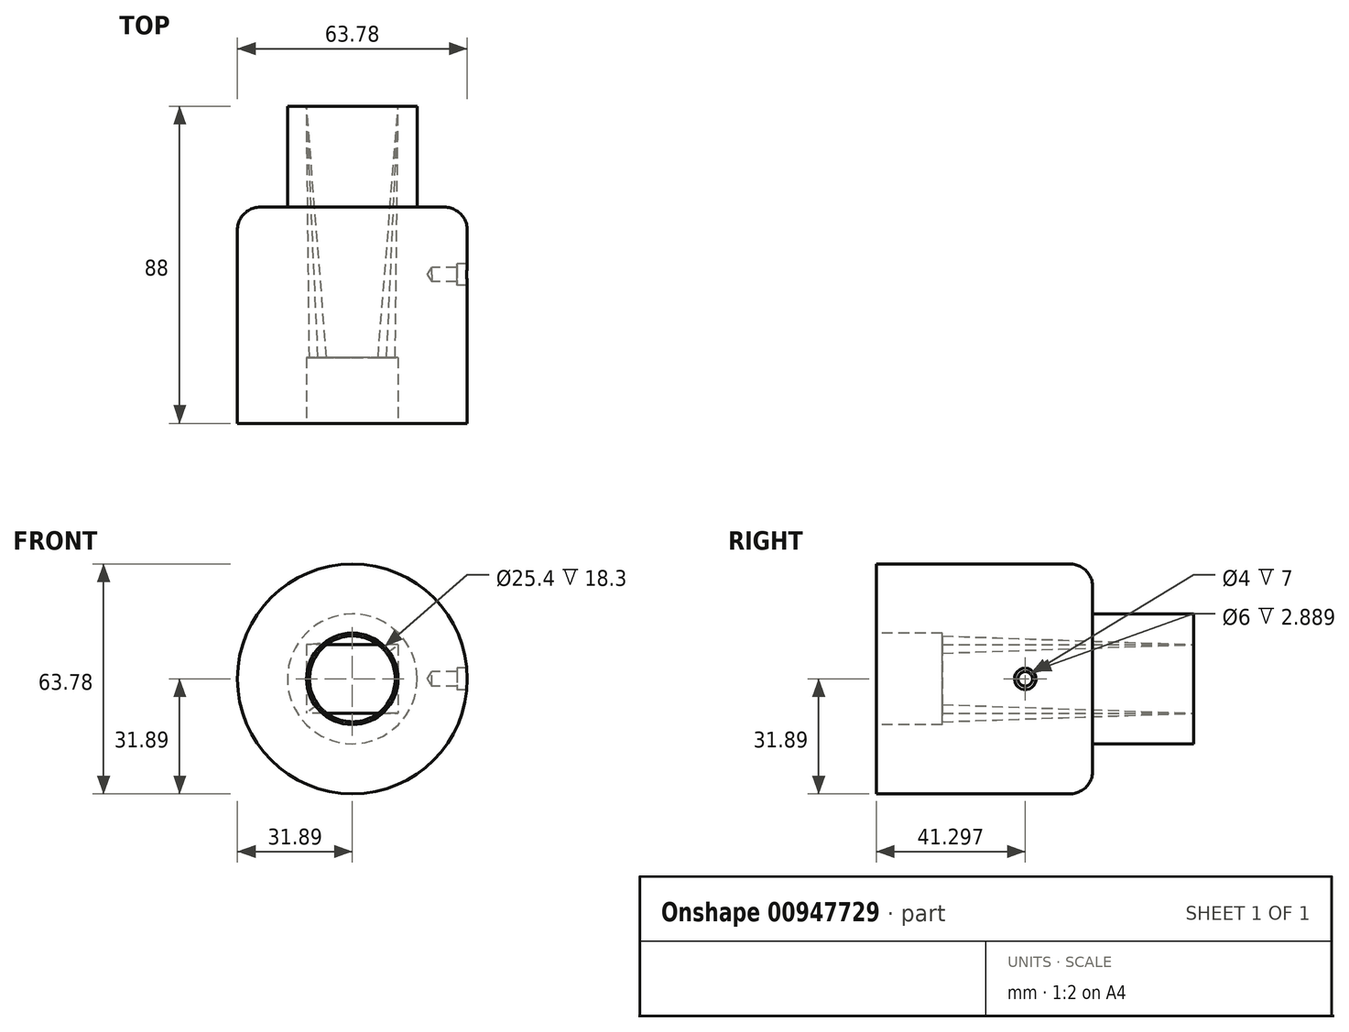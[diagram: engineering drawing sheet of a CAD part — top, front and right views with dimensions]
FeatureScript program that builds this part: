
annotation { "Feature Type Name" : "Feature", "Feature Type Description" : "" }
export const myFeature = defineFeature(function(context is Context, id is Id, definition is map)
    precondition{}
    {
        {
            var Q0;
            Q0=qCreatedBy(makeId("Right.planeOp"),FACE);
            var sketch = newSketch(context, id + "F0", { "sketchPlane" : qUnion([Q0])});
            skLineSegment(sketch, "E0", {"start": v(-91.81, 0) * mm, "end": v(-91.81, 31.89) * mm});
            skLineSegment(sketch, "E1", {"start": v(-91.81, 31.89) * mm, "end": v(-38.16, 31.89) * mm});
            skLineSegment(sketch, "E2", {"start": v(-91.81, 0) * mm, "end": v(-3.81, 0) * mm});
            skLineSegment(sketch, "E3", {"start": v(-3.81, 0) * mm, "end": v(-3.81, 18) * mm});
            skLineSegment(sketch, "E4", {"start": v(-3.81, 18) * mm, "end": v(-31.81, 18) * mm});
            skLineSegment(sketch, "E5", {"start": v(-31.81, 18) * mm, "end": v(-31.81, 25.54) * mm});
            skPoint(sketch, "E6.visualSharp", {"position": v(-31.81, 31.89) * mm});
            skArc(sketch, "E6.filletArc", {"start": v(-31.81, 25.54) * mm, "mid": v(-33.67, 30.03) * mm, "end": v(-38.16, 31.89) * mm});
            skSolve(sketch);
        }
        {
            var Q0;
            Q0=qSketchRegion(id+"F0",true);
            var Q1;
            Q1=sQuery(id+"F0.wireOp",EDGE,"E2");
            revolve(context, id + "F1", {"entities" : qUnion([Q0]), "axis" : qUnion([Q1]), "revolveType" : RevolveType.FULL});
        }
        {
            var Q0;
            Q0=makeQuery(id+"F1.opRevolve","SWEPT_FACE",FACE,{"disambiguationData":[OSD([sQuery(id+"F0.wireOp",EDGE,"E3")])]});
            var sketch = newSketch(context, id + "F2", { "sketchPlane" : qUnion([Q0])});
            skLineSegment(sketch, "E7.bottom", {"start": v(-12.7, 9.52) * mm, "end": v(12.7, 9.52) * mm});
            skLineSegment(sketch, "E7.top", {"start": v(-12.7, -9.53) * mm, "end": v(12.7, -9.53) * mm});
            skLineSegment(sketch, "E7.left", {"start": v(-12.7, 9.52) * mm, "end": v(-12.7, -9.52) * mm});
            skLineSegment(sketch, "E7.right", {"start": v(12.7, 9.52) * mm, "end": v(12.7, -9.53) * mm});
            skSolve(sketch);
        }
        {
            var Q0;
            Q0=makeQuery(id+"F1.opRevolve","SWEPT_FACE",FACE,{"disambiguationData":[OSD([sQuery(id+"F0.wireOp",EDGE,"E0")])]});
            var sketch = newSketch(context, id + "F3", { "sketchPlane" : qUnion([Q0])});
            skCircle(sketch, "E8", {"center": v(0, 0) * mm, "radius": 12.7 * mm});
            skSolve(sketch);
        }
        {
            var Q0;
            Q0=qSketchRegion(id+"F3",true);
            extrude(context, id + "F4", {"entities" : qUnion([Q0]), "operationType" : NewBodyOperationType.REMOVE, "oppositeDirection" : true, "depth" : 18.3 * mm});
        }
        {
            var Q0;
            Q0=makeQuery(id+"F4.boolean.opBoolean","COPY",FACE,{"derivedFrom":makeQuery(id+"F4.opExtrude","CAP_FACE",FACE,{"disambiguationData":[OSD([sQuery(id+"F3.wireOp",EDGE,"E8")])],"isStart":false})});
            var sketch = newSketch(context, id + "F5", { "sketchPlane" : qUnion([Q0])});
            skCircle(sketch, "E9", {"center": v(0, 0) * mm, "radius": 11.9 * mm});
            skSolve(sketch);
        }
        {
            var Q1;
            Q1=qSketchRegion(id+"F5",true);
            var Q2;
            Q2=qSketchRegion(id+"F2",true);
            loft(context, id + "F6", {"operationType" : NewBodyOperationType.REMOVE, "sheetProfilesArray" : [{ "sheetProfileEntities" : qUnion([Q1]) }, { "sheetProfileEntities" : qUnion([Q2]) }]});
        }
        {
            var Q0;
            Q0=qCreatedBy(makeId("Right.planeOp"),FACE);
            cPlane(context, id + "F7", {"entities" : qUnion([Q0]), "cplaneType" : CPlaneType.OFFSET, "offset" : 32 * mm, "width" : 150 * mm, "height" : 150 * mm});
        }
        {
            var Q0;
            Q0=qCreatedBy(id+"F7.planeOp",FACE);
            var sketch = newSketch(context, id + "F8", { "sketchPlane" : qUnion([Q0])});
            skLineSegment(sketch, "E10", {"start": v(0, 0) * mm, "end": v(-115.51, 0) * mm, "construction": true});
            skPoint(sketch, "E11", {"position": v(-50.51, 0) * mm});
            skSolve(sketch);
        }
        {
            var Q0;
            Q0=sQuery(id+"F8.wireOp",VERTEX,"E11");
            var Q1;
            Q1=makeQuery(id+"F1.opRevolve","SWEPT_BODY",BODY,{"disambiguationData":[OSD([sQuery(id+"F0.wireOp",EDGE,"E0"),sQuery(id+"F0.wireOp",EDGE,"E1"),sQuery(id+"F0.wireOp",EDGE,"E2"),sQuery(id+"F0.wireOp",EDGE,"E3"),sQuery(id+"F0.wireOp",EDGE,"E4"),sQuery(id+"F0.wireOp",EDGE,"E5"),sQuery(id+"F0.wireOp",EDGE,"E6.filletArc")])]});
            hole(context, id + "F9", {"style" : HoleStyle.C_BORE, "endStyle" : HoleEndStyle.BLIND, "holeDiameter" : 4 * mm, "cBoreDiameter" : 6 * mm, "cBoreDepth" : 3 * mm, "holeDepth" : 10 * mm, "isTappedThrough" : true, "tappedDepth" : 46.25 * mm, "tapClearance" : 3, "locations" : qUnion([Q0]), "scope" : qUnion([Q1]), "startStyle" : HoleStartStyle.SKETCH});
        }
    });
